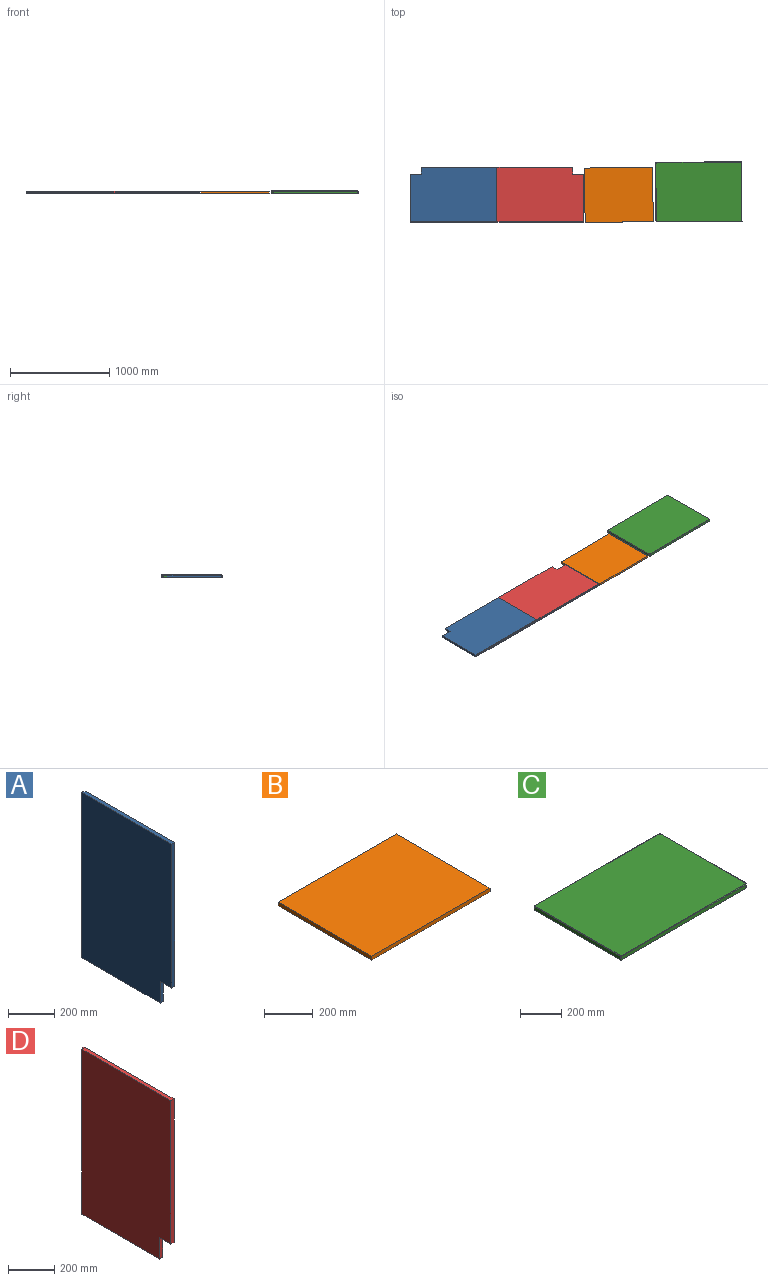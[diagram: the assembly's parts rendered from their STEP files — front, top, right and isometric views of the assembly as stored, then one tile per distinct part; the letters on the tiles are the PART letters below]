
ASSEMBLY  parts=4 mates=3
PART A: 10 faces, bbox 19.1x552.5x876.3 mm
  f0: plane 552.45x19.05mm, normal (0,0,1), area 10463.7mm2, adj f1,f3,f5,f7,f8,f9
  f1: plane 876.3x546.1mm, normal (1,0,0), area 470563.6mm2, adj f0,f2,f4,f6,f7,f9
  f2: plane 482.6x19.05mm, normal (0,0,-1), area 9133mm2, adj f1,f3,f5,f6,f8,f9
  f3: plane 876.3x552.45mm, normal (-1,0,0), area 476128.1mm2, adj f0,f2,f4,f5,f6,f7
  f4: plane 69.85x19.05mm, normal (0,0,-1), area 1330.6mm2, adj f1,f3,f6,f7
  f5: plane 876.3x9.53mm, normal (0,1,0), area 8346.8mm2, adj f0,f2,f3,f8
  f6: plane 114.3x19.05mm, normal (0,-1,0), area 2177.4mm2, adj f1,f2,f3,f4
  f7: plane 762x19.05mm, normal (0,-1,0), area 14516.1mm2, adj f0,f1,f3,f4
  f8: plane 876.3x6.35mm, normal (1,0,0), area 5564.5mm2, adj f0,f2,f5,f9
  f9: plane 876.3x9.53mm, normal (0,1,0), area 8346.8mm2, adj f0,f1,f2,f8
PART B: 6 faces, bbox 685.8x546.1x19.1 mm
  f0: plane 546.1x19.05mm, normal (-1,0,0), area 10403.2mm2, adj f1,f3,f4,f5
  f1: plane 685.8x19.05mm, normal (0,-1,0), area 13064.5mm2, adj f0,f2,f4,f5
  f2: plane 546.1x19.05mm, normal (1,0,0), area 10403.2mm2, adj f1,f3,f4,f5
  f3: plane 685.8x19.05mm, normal (0,1,0), area 13064.5mm2, adj f0,f2,f4,f5
  f4: plane 685.8x546.1mm, normal (0,0,-1), area 374515.4mm2, adj f0,f1,f2,f3
  f5: plane 685.8x546.1mm, normal (0,0,1), area 374515.4mm2, adj f0,f1,f2,f3
PART C: 18 faces, bbox 867.8x602.2x23.8 mm
  f0: cylinder r=12.7mm len=21.27mm, axis (0,0,-1), area 424.4mm2, adj f1,f7,f9,f15
  f1: plane 851.54x21.27mm, normal (0,1,0), area 18114.3mm2, adj f0,f2,f9,f13
  f2: cylinder r=2.54mm len=21.27mm, axis (0,0,1), area 84.9mm2, adj f1,f3,f9,f11
  f3: plane 595x21.27mm, normal (-1,0,0), area 12657mm2, adj f2,f4,f9,f10
  f4: cylinder r=2.54mm len=21.27mm, axis (0,0,-1), area 84.9mm2, adj f3,f5,f9,f12
  f5: plane 851.54x21.27mm, normal (0,-1,0), area 18114.3mm2, adj f4,f6,f9,f14
  f6: cylinder r=12.7mm len=21.27mm, axis (0,0,-1), area 424.4mm2, adj f5,f7,f9,f16
  f7: plane 574.68x21.27mm, normal (1,0,0), area 12224.8mm2, adj f0,f6,f9,f17
  f8: plane 861.7x595mm, normal (0,0,1), area 512659.9mm2, adj f10,f13,f14,f15,f16,f17
  f9: plane 866.78x600.08mm, normal (0,0,-1), area 520058mm2, adj f0,f1,f2,f3,f4,f5,f6,f7
  f10: cylinder r=2.54mm len=595mm, axis (0,1,0), area 2373.9mm2, adj f3,f8,f11,f12
  f11: sphere r=2.54mm, area 10.1mm2, adj f2,f10,f13
  f12: sphere r=2.54mm, area 10.1mm2, adj f4,f10,f14
  f13: cylinder r=2.54mm len=851.54mm, axis (1,0,0), area 3397.5mm2, adj f1,f8,f11,f15
  f14: cylinder r=2.54mm len=851.54mm, axis (-1,0,0), area 3397.5mm2, adj f5,f8,f12,f16
  f15: torus R=10.16mm, axis (0,0,1), area 73.8mm2, adj f0,f8,f13,f17
  f16: torus R=10.16mm, axis (0,0,1), area 73.8mm2, adj f6,f8,f14,f17
  f17: cylinder r=2.54mm len=574.68mm, axis (0,-1,0), area 2292.9mm2, adj f7,f8,f15,f16
PART D: 10 faces, bbox 19.1x552.5x876.3 mm
  f0: plane 552.45x19.05mm, normal (0,0,1), area 10463.7mm2, adj f1,f3,f5,f7,f8,f9
  f1: plane 876.3x546.1mm, normal (-1,0,0), area 470563.6mm2, adj f0,f2,f4,f6,f7,f9
  f2: plane 482.6x19.05mm, normal (0,0,-1), area 9133mm2, adj f1,f3,f5,f6,f8,f9
  f3: plane 876.3x552.45mm, normal (1,0,0), area 476128.1mm2, adj f0,f2,f4,f5,f6,f7
  f4: plane 69.85x19.05mm, normal (0,0,-1), area 1330.6mm2, adj f1,f3,f6,f7
  f5: plane 876.3x9.53mm, normal (0,1,0), area 8346.8mm2, adj f0,f2,f3,f8
  f6: plane 114.3x19.05mm, normal (0,-1,0), area 2177.4mm2, adj f1,f2,f3,f4
  f7: plane 762x19.05mm, normal (0,-1,0), area 14516.1mm2, adj f0,f1,f3,f4
  f8: plane 876.3x6.35mm, normal (-1,0,0), area 5564.5mm2, adj f0,f2,f5,f9
  f9: plane 876.3x9.53mm, normal (0,1,0), area 8346.8mm2, adj f0,f1,f2,f8
PLACE A rot(axis=(-0.71,0,-0.71),180deg) t=(-603.51,-563.9,-171.4)mm
PLACE B rot(axis=(0,0,-1),179.6deg) t=(1503.16,-568.86,-666.7)mm
PLACE C rot(axis=(0,0,-1),179.6deg) t=(2308.02,-558.25,-1409.65)mm
PLACE D rot(axis=(-0.71,0,0.71),180deg) t=(1149.09,-563.9,-171.4)mm
MATE fastened A.f0 <-> D.f0  axis (1,0,0) through (272.79,-11.45,-533.35)mm
MATE planar C.f9 <-> D.f3  axis (0,0,-1) through (2306.12,-258.22,-533.35)mm
MATE planar C.f9 <-> B.f4  axis (0,0,-1) through (2306.12,-258.22,-533.35)mm
